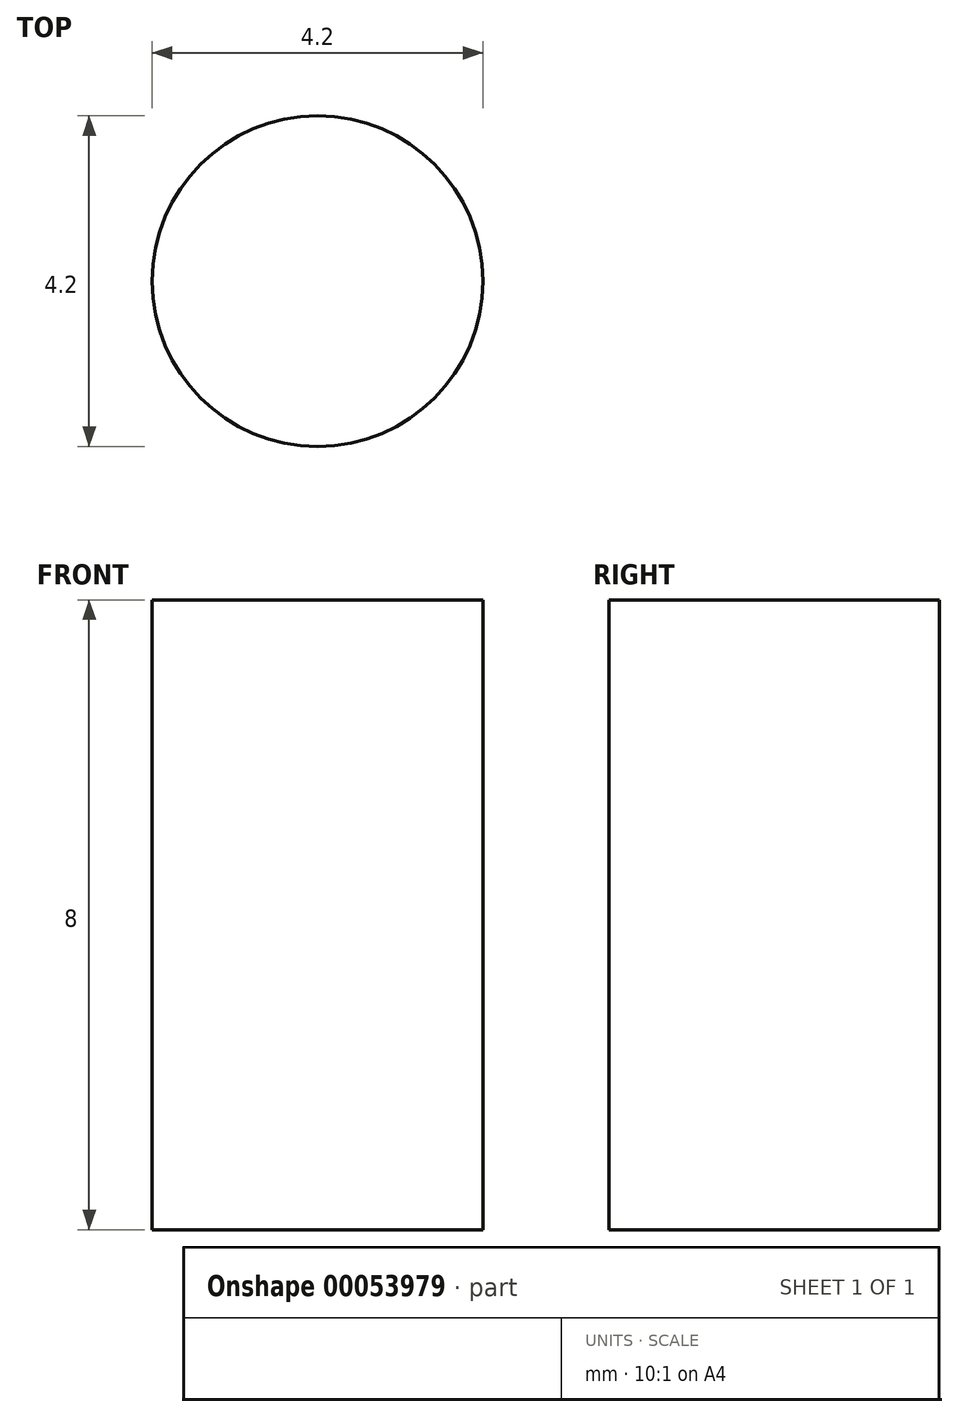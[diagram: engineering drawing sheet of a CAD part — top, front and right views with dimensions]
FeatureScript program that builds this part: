
annotation { "Feature Type Name" : "Feature", "Feature Type Description" : "" }
export const myFeature = defineFeature(function(context is Context, id is Id, definition is map)
    precondition{}
    {
        {
            var Q0;
            Q0=qCreatedBy(makeId("Top.planeOp"),FACE);
            var sketch = newSketch(context, id + "F0", { "sketchPlane" : qUnion([Q0])});
            skCircle(sketch, "E0", {"center": v(0, 0) * mm, "radius": 2.1 * mm});
            skSolve(sketch);
        }
        {
            var Q0;
            Q0=sQuery(id+"F0.wireOp",EDGE,"E0");
            extrude(context, id + "F1", {"bodyType" : ToolBodyType.SURFACE, "surfaceEntities" : qUnion([Q0]), "depth" : 8 * mm});
        }
    });
